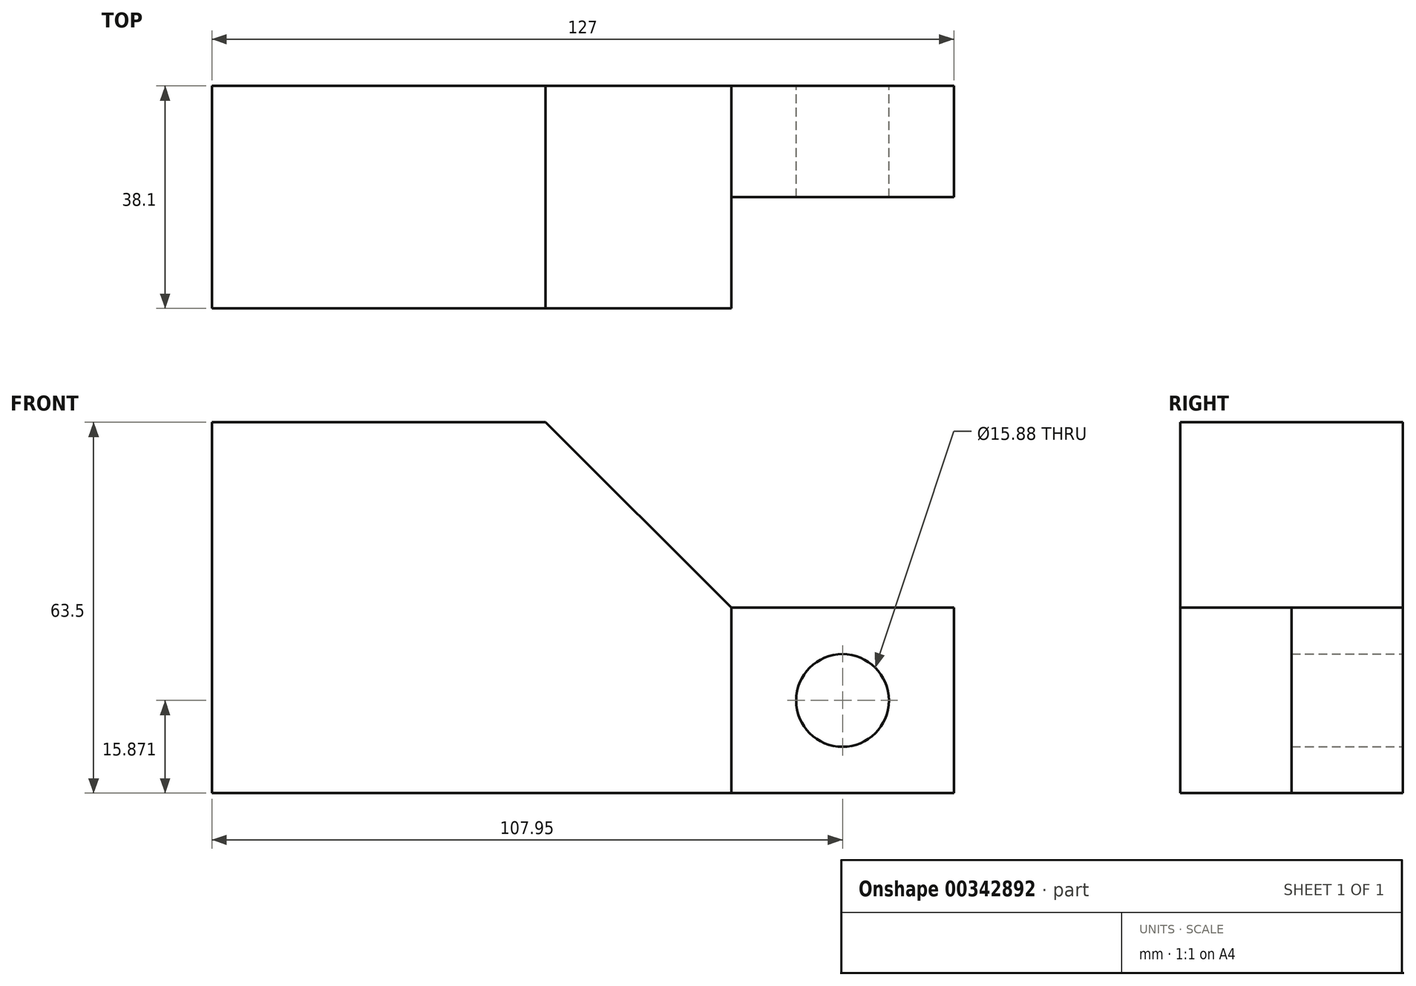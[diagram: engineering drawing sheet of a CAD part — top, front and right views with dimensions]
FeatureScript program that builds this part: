
annotation { "Feature Type Name" : "Feature", "Feature Type Description" : "" }
export const myFeature = defineFeature(function(context is Context, id is Id, definition is map)
    precondition{}
    {
        {
            var Q0;
            Q0=qCreatedBy(makeId("Front.planeOp"),FACE);
            var sketch = newSketch(context, id + "F0", { "sketchPlane" : qUnion([Q0])});
            skPoint(sketch, "E0.start.orphan", {"position": v(-30.03, 0) * mm});
            skLineSegment(sketch, "E1", {"start": v(-57.15, -30.41) * mm, "end": v(69.85, -30.41) * mm});
            skLineSegment(sketch, "E2", {"start": v(-57.15, -30.41) * mm, "end": v(-57.15, 33.09) * mm});
            skLineSegment(sketch, "E3", {"start": v(69.85, -30.41) * mm, "end": v(69.85, 1.34) * mm});
            skLineSegment(sketch, "E4", {"start": v(69.85, 1.34) * mm, "end": v(31.75, 1.34) * mm});
            skLineSegment(sketch, "E5", {"start": v(31.75, 1.34) * mm, "end": v(0, 33.09) * mm});
            skLineSegment(sketch, "E6", {"start": v(-57.15, 33.09) * mm, "end": v(0, 33.09) * mm});
            skLineSegment(sketch, "E7", {"start": v(31.75, 1.34) * mm, "end": v(31.75, -30.41) * mm});
            skCircle(sketch, "E8", {"center": v(50.8, -14.54) * mm, "radius": 7.94 * mm});
            skPoint(sketch, "E8.centerSnap0", {"position": v(69.85, -14.54) * mm});
            skPoint(sketch, "E8.centerSnap1", {"position": v(50.8, 1.34) * mm});
            skSolve(sketch);
        }
        {
            var Q0;
            {var subQ0=sQuery(id+"F0.wireOp",EDGE,"E2");Q0=makeQuery(id+"F0.imprint","IMPRINT",FACE,{"disambiguationData":[TD([[makeQuery(id+"F0.imprint","IMPRINT",EDGE,{"derivedFrom":subQ0}),-1.0]])]});}
            extrude(context, id + "F1", {"entities" : qUnion([Q0]), "depth" : 38.1 * mm});
        }
        {
            var Q0;
            {var subQ1=sQuery(id+"F0.wireOp",EDGE,"E3");Q0=makeQuery(id+"F0.imprint","IMPRINT",FACE,{"disambiguationData":[TD([[makeQuery(id+"F0.imprint","IMPRINT",EDGE,{"derivedFrom":subQ1}),1.0]])]});}
            extrude(context, id + "F2", {"entities" : qUnion([Q0]), "operationType" : NewBodyOperationType.ADD, "depth" : 19.05 * mm});
        }
    });
